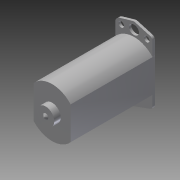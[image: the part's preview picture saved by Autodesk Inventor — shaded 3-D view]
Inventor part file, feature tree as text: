
AUTODESK INVENTOR PART (.ipt)
format: ipt  version: 2014 SP1 (Build 180222100, 222)  size: 100,864 bytes
history: native  units: in
note: dims shown in document units (in); Inventor stores cm internally (conversion verified against a paired STEP export)
features: other x2, imported_body x2, fillet x1
ambient origin geometry x8: Origin, YZ Plane, XZ Plane, XY Plane, X Axis, Y Axis, Z Axis, Center Point
bodies: Body1 (feature_tree), Body2 (feature_tree)
feature tree (5):
  fillet  "Fillet1"  [1 undecoded]
  other  "AM-2235 motor1"
  other  "Boss-Extrude4"
  imported_body  "Base1"
  imported_body  "Base2"
note: 1 required parameter value undecoded (feature->parameter linkage not recoverable at this tier; creation-order binding heuristic only, values carry confidence <= 0.55)
